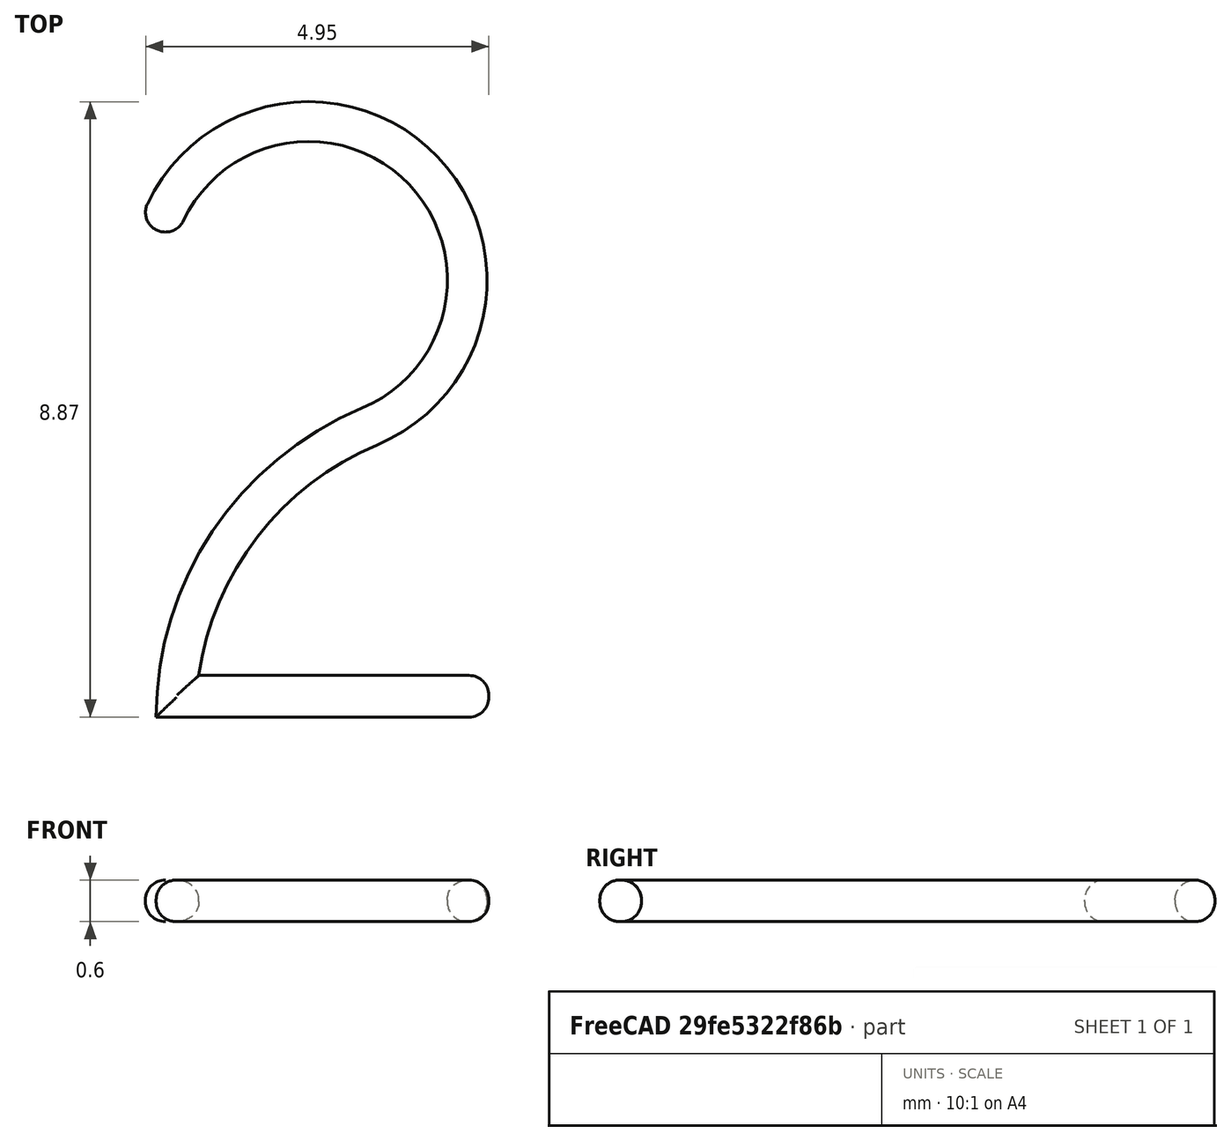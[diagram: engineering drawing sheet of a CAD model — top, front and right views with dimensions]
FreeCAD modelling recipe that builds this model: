
FCSTD DOCUMENT  (FreeCAD 0.16R6712 (Git))
Label: 2s
License: All rights reserved
LicenseURL: http://en.wikipedia.org/wiki/All_rights_reserved
objects: Sketcher::SketchObject×1, PartDesign::Pad×1, PartDesign::Fillet×1, Mesh::Feature×1
note: 4 computed .brp shape members not serialized (recipe doc carries the construction recipe); baked Part::Feature solids carry a one-line shape summary decoded from their .brp

FEATURE [Sketcher::SketchObject] Sketch
  sketch-geometry (8):
    g0: ArcOfCircle CenterX=0 CenterY=6.3 CenterZ=0 NormalX=0 NormalY=0 NormalZ=1 Radius=2 StartAngle=5.10717 EndAngle=9.0722
    g1: LineSegment StartX=-2.2 StartY=0 StartZ=0 EndX=2.6 EndY=0 EndZ=0
    g2: ArcOfCircle CenterX=2.625 CenterY=0 CenterZ=0 NormalX=0 NormalY=0 NormalZ=1 Radius=4.825 StartAngle=1.96559 EndAngle=3.14159
    g3: ArcOfCircle CenterX=0 CenterY=6.3 CenterZ=0 NormalX=0 NormalY=0 NormalZ=1 Radius=2.57312 StartAngle=5.10717 EndAngle=9.15054
    g4: LineSegment StartX=2.6 StartY=0.6 StartZ=0 EndX=-1.58433 EndY=0.6 EndZ=0
    g5: LineSegment StartX=-2.47697 StartY=6.99684 StartZ=0 EndX=-1.87697 EndY=6.99064 EndZ=0
    g6: LineSegment StartX=2.6 StartY=0 StartZ=0 EndX=2.6 EndY=0.6 EndZ=0
    g7: ArcOfCircle CenterX=2.625 CenterY=0 CenterZ=0 NormalX=0 NormalY=0 NormalZ=1 Radius=4.25188 StartAngle=1.96559 EndAngle=3.00001
  constraints (25):
    c: PointOnObject(g0,g-2)
    c: PointOnObject(g1,g-1)
    c: PointOnObject(g1,g-1)
    c: Coincident(g2,g1)
    c: Radius(g0) = 2
    c: Coincident(g2,g0)
    c: DistanceY(g-1,g0) = 6.3
    c: Tangent(g0,g2)
    c: DistanceX(g-2,g1) = -2.2
    c: Distance(g-1,g1) = 2.6
    c: Coincident(g3,g0)
    c: Horizontal(g4)
    c: Coincident(g5,g3)
    c: Coincident(g5,g0)
    c: Coincident(g6,g1)
    c: Coincident(g6,g4)
    c: Vertical(g6)
    c: DistanceX(g3,g0) = 0.6
    c: DistanceY(g-1,g4) = 0.6
    c: Perpendicular(g2,g1)
    c: Coincident(g7,g2)
    c: Coincident(g7,g3)
    c: PointOnObject(g7,g4)
    c: Coincident(g4,g7)
    c: Tangent(g3,g7)
FEATURE [PartDesign::Pad] Pad
  Length = 0.6
  Length2 = 100
  Midplane = true
  Sketch = -> Sketch
  Type = 0
FEATURE [PartDesign::Fillet] Fillet
  Base = -> Pad [Edge3,Edge6,Edge9,Edge12,Edge15,Edge18,Edge21,Edge23,Edge20,Edge17,Edge22,Edge4,Edge7,Edge10,Edge13,Edge16,Edge19,Edge24,Edge8,Edge5]
  Radius = 0.285
FEATURE [Mesh::Feature] Mesh  label="Fillet (Meshed)"
